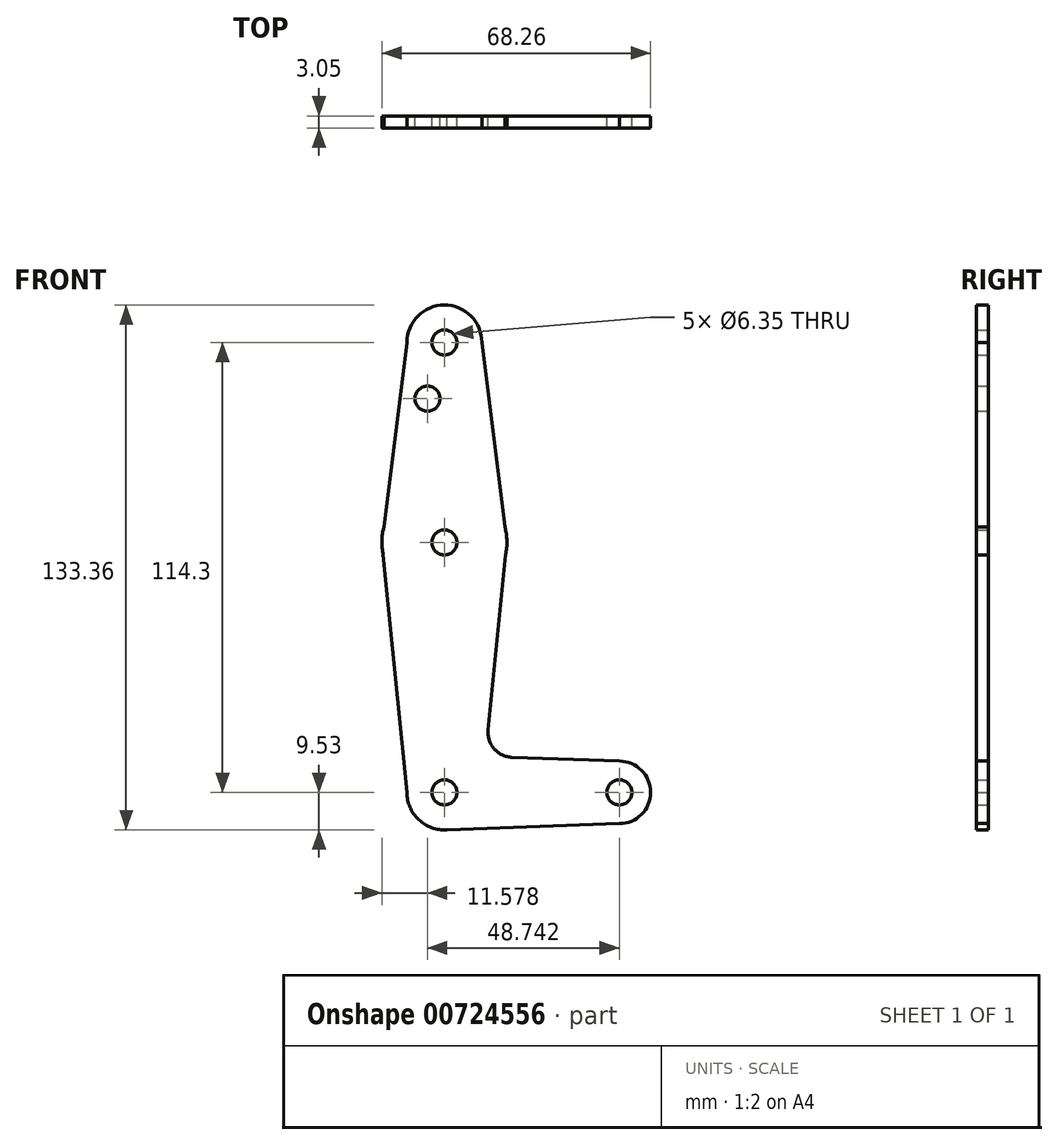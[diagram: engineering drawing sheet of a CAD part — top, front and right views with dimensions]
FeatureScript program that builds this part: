
annotation { "Feature Type Name" : "Feature", "Feature Type Description" : "" }
export const myFeature = defineFeature(function(context is Context, id is Id, definition is map)
    precondition{}
    {
        {
            var Q0;
            Q0=qCreatedBy(makeId("Front.planeOp"),FACE);
            var sketch = newSketch(context, id + "F0", { "sketchPlane" : qUnion([Q0])});
            skLineSegment(sketch, "E0", {"start": v(0, 0) * mm, "end": v(0, 114.3) * mm, "construction": true});
            skLineSegment(sketch, "E1", {"start": v(0, 0) * mm, "end": v(44.45, 0) * mm, "construction": true});
            skCircle(sketch, "E2", {"center": v(0, 0) * mm, "radius": 9.52 * mm});
            skCircle(sketch, "E3", {"center": v(0, 114.3) * mm, "radius": 9.52 * mm});
            skCircle(sketch, "E4", {"center": v(44.45, 0) * mm, "radius": 7.94 * mm});
            skCircle(sketch, "E5", {"center": v(0, 63.5) * mm, "radius": 15.88 * mm});
            skLineSegment(sketch, "E6", {"start": v(-15.88, 63.5) * mm, "end": v(-9.52, 114.3) * mm});
            skLineSegment(sketch, "E7", {"start": v(9.52, 114.3) * mm, "end": v(15.88, 63.5) * mm});
            skLineSegment(sketch, "E8", {"start": v(15.88, 63.5) * mm, "end": v(11.11, 15.89) * mm});
            skLineSegment(sketch, "E9", {"start": v(-9.52, 0) * mm, "end": v(-15.88, 63.5) * mm});
            skLineSegment(sketch, "E10", {"start": v(17.2, 8.91) * mm, "end": v(44.45, 7.94) * mm});
            skLineSegment(sketch, "E11", {"start": v(0, -9.52) * mm, "end": v(44.45, -7.94) * mm});
            skArc(sketch, "E12.filletArc", {"start": v(11.11, 15.89) * mm, "mid": v(12.65, 11.08) * mm, "end": v(17.2, 8.91) * mm});
            skCircle(sketch, "E13", {"center": v(0, 114.3) * mm, "radius": 3.18 * mm});
            skCircle(sketch, "E14", {"center": v(0, 63.5) * mm, "radius": 3.18 * mm});
            skCircle(sketch, "E15", {"center": v(0, 0) * mm, "radius": 3.18 * mm});
            skCircle(sketch, "E16", {"center": v(44.45, 0) * mm, "radius": 3.18 * mm});
            skPoint(sketch, "E17.center.orphan", {"position": v(-1.59, 100.03) * mm});
            skCircle(sketch, "E18", {"center": v(-4.3, 100.03) * mm, "radius": 3.18 * mm});
            skSolve(sketch);
        }
        {
            var Q0;
            Q0 = qSketchRegion(id + "F0", true);
            extrude(context, id + "F1", {"entities" : qUnion([Q0]), "depth" : 3.05 * mm, "offsetDistance" : 25.4 * mm});
        }
    });
